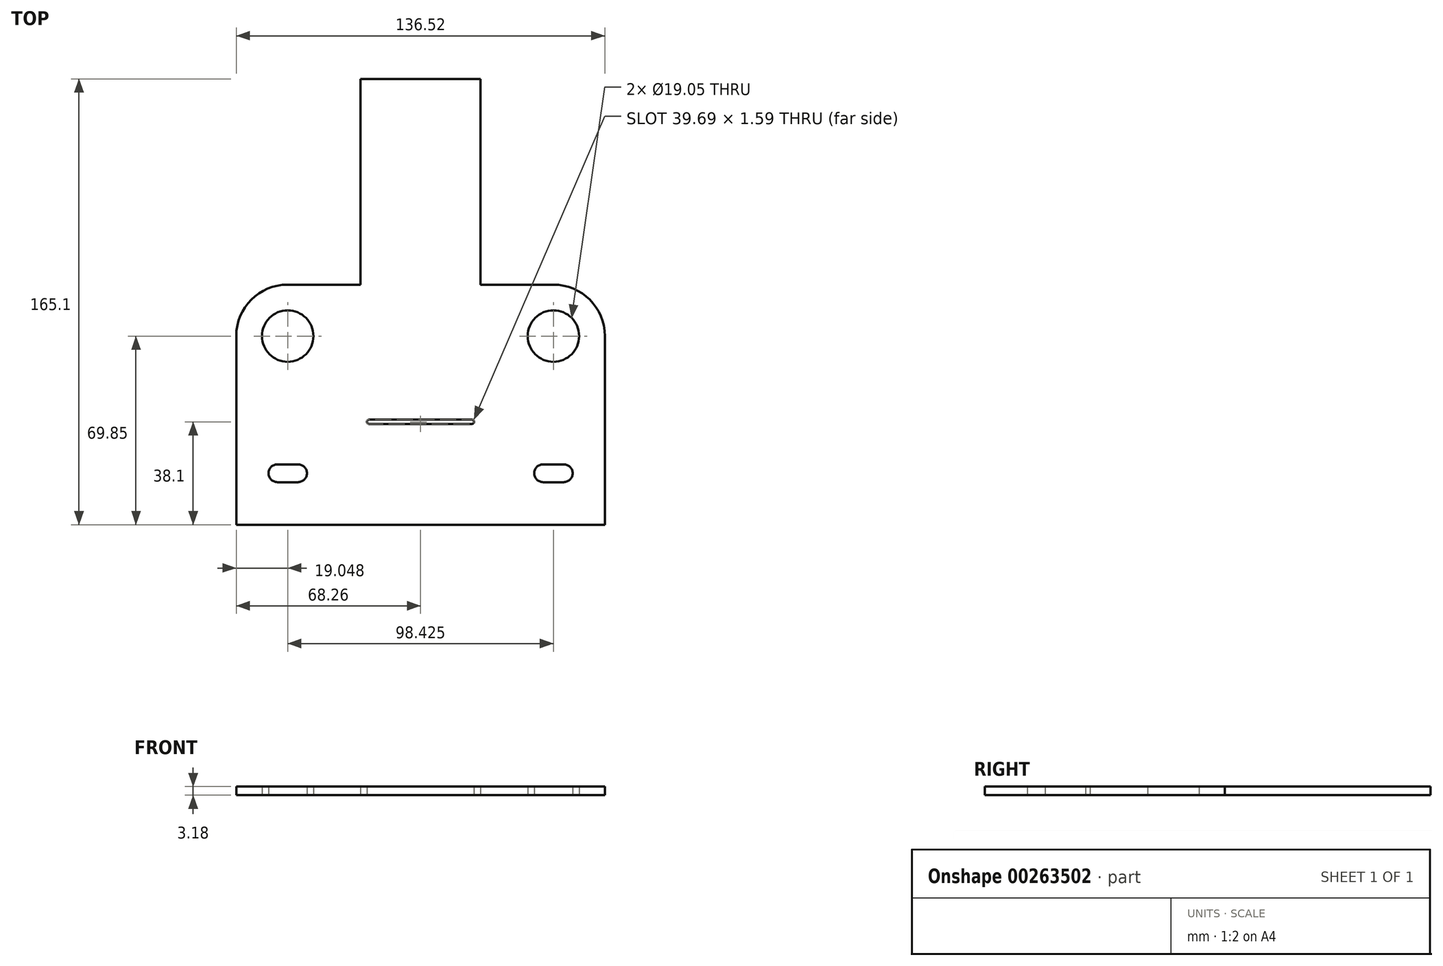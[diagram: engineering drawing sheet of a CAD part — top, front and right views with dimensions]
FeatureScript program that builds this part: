
annotation { "Feature Type Name" : "Feature", "Feature Type Description" : "" }
export const myFeature = defineFeature(function(context is Context, id is Id, definition is map)
    precondition{}
    {
        {
            var Q0;
            Q0=qCreatedBy(makeId("Top.planeOp"),FACE);
            var sketch = newSketch(context, id + "F0", { "sketchPlane" : qUnion([Q0])});
            skLineSegment(sketch, "E0.bottom", {"start": v(68.26, -19.05) * mm, "end": v(-68.26, -19.05) * mm});
            skLineSegment(sketch, "E0.top", {"start": v(68.26, 19.05) * mm, "end": v(-68.26, 19.05) * mm, "construction": true});
            skLineSegment(sketch, "E0.left", {"start": v(68.26, -19.05) * mm, "end": v(68.26, 19.05) * mm});
            skLineSegment(sketch, "E0.right", {"start": v(-68.26, -19.05) * mm, "end": v(-68.26, 19.05) * mm});
            skPoint(sketch, "E0.middle", {"position": v(0, 0) * mm});
            skLineSegment(sketch, "E1.top", {"start": v(-49.21, 69.85) * mm, "end": v(49.21, 69.85) * mm});
            skLineSegment(sketch, "E1.left", {"start": v(-68.26, 19.05) * mm, "end": v(-68.26, 50.8) * mm});
            skLineSegment(sketch, "E1.right", {"start": v(68.26, 19.05) * mm, "end": v(68.26, 50.8) * mm});
            skLineSegment(sketch, "E2.bottom", {"start": v(-22.23, 69.85) * mm, "end": v(22.23, 69.85) * mm});
            skLineSegment(sketch, "E2.top", {"start": v(-22.22, 146.05) * mm, "end": v(22.22, 146.05) * mm});
            skLineSegment(sketch, "E2.left", {"start": v(-22.23, 69.85) * mm, "end": v(-22.22, 146.05) * mm});
            skLineSegment(sketch, "E2.right", {"start": v(22.22, 69.85) * mm, "end": v(22.23, 146.05) * mm});
            skLineSegment(sketch, "E3", {"start": v(-49.21, 0) * mm, "end": v(49.21, 0) * mm, "construction": true});
            skCircle(sketch, "E4", {"center": v(-49.21, 0) * mm, "radius": 3.3 * mm, "construction": true});
            skCircle(sketch, "E5", {"center": v(49.21, 0) * mm, "radius": 3.3 * mm, "construction": true});
            skLineSegment(sketch, "E6", {"start": v(-49.21, 0) * mm, "end": v(-68.26, 0) * mm, "construction": true});
            skLineSegment(sketch, "E7", {"start": v(-53.02, 0) * mm, "end": v(-45.4, 0) * mm});
            skArc(sketch, "E8.0.startCap", {"start": v(-53.02, -3.3) * mm, "mid": v(-56.32, 0) * mm, "end": v(-53.02, 3.3) * mm});
            skArc(sketch, "E8.0.endCap", {"start": v(-45.4, 3.3) * mm, "mid": v(-42.1, 0) * mm, "end": v(-45.4, -3.3) * mm});
            skLineSegment(sketch, "E8.0.left", {"start": v(-53.02, 3.3) * mm, "end": v(-45.4, 3.3) * mm});
            skLineSegment(sketch, "E8.0.right", {"start": v(-53.02, -3.3) * mm, "end": v(-45.4, -3.3) * mm});
            skLineSegment(sketch, "E9", {"start": v(0, 19.05) * mm, "end": v(0, -19.05) * mm, "construction": true});
            skLineSegment(sketch, "E10.MirrorCS", {"start": v(53.02, 3.3) * mm, "end": v(45.4, 3.3) * mm});
            skArc(sketch, "E11.MirrorCS", {"start": v(53.02, -3.3) * mm, "mid": v(56.32, 0) * mm, "end": v(53.02, 3.3) * mm});
            skLineSegment(sketch, "E12.MirrorCS", {"start": v(53.02, -3.3) * mm, "end": v(45.4, -3.3) * mm});
            skArc(sketch, "E13.MirrorCS", {"start": v(45.4, 3.3) * mm, "mid": v(42.1, 0) * mm, "end": v(45.4, -3.3) * mm});
            skLineSegment(sketch, "E14", {"start": v(0, 146.05) * mm, "end": v(0, 69.85) * mm});
            skLineSegment(sketch, "E15", {"start": v(-49.21, 69.85) * mm, "end": v(-49.21, 50.8) * mm});
            skLineSegment(sketch, "E16", {"start": v(-49.21, 50.8) * mm, "end": v(49.21, 50.8) * mm});
            skLineSegment(sketch, "E17", {"start": v(49.21, 50.8) * mm, "end": v(49.21, 69.85) * mm});
            skCircle(sketch, "E18", {"center": v(-49.21, 50.8) * mm, "radius": 9.53 * mm});
            skCircle(sketch, "E19", {"center": v(49.21, 50.8) * mm, "radius": 9.53 * mm});
            skPoint(sketch, "E20.visualSharp", {"position": v(-68.26, 69.85) * mm});
            skArc(sketch, "E20.filletArc", {"start": v(-49.21, 69.85) * mm, "mid": v(-62.68, 64.27) * mm, "end": v(-68.26, 50.8) * mm});
            skPoint(sketch, "E21.visualSharp", {"position": v(68.26, 69.85) * mm});
            skArc(sketch, "E21.filletArc", {"start": v(68.26, 50.8) * mm, "mid": v(62.68, 64.27) * mm, "end": v(49.21, 69.85) * mm});
            skLineSegment(sketch, "E22", {"start": v(-19.05, 19.05) * mm, "end": v(19.05, 19.05) * mm});
            skArc(sketch, "E23.0.startCap", {"start": v(-19.05, 18.26) * mm, "mid": v(-19.84, 19.05) * mm, "end": v(-19.05, 19.84) * mm});
            skArc(sketch, "E23.0.endCap", {"start": v(19.05, 19.84) * mm, "mid": v(19.84, 19.05) * mm, "end": v(19.05, 18.26) * mm});
            skLineSegment(sketch, "E23.0.left", {"start": v(-19.05, 19.84) * mm, "end": v(19.05, 19.84) * mm});
            skLineSegment(sketch, "E23.0.right", {"start": v(-19.05, 18.26) * mm, "end": v(19.05, 18.26) * mm});
            skSolve(sketch);
        }
        {
            var Q0;
            Q0 = qSketchRegion(id + "F0", true);
            extrude(context, id + "F1", {"entities" : qUnion([Q0]), "depth" : 3.17 * mm});
        }
    });
